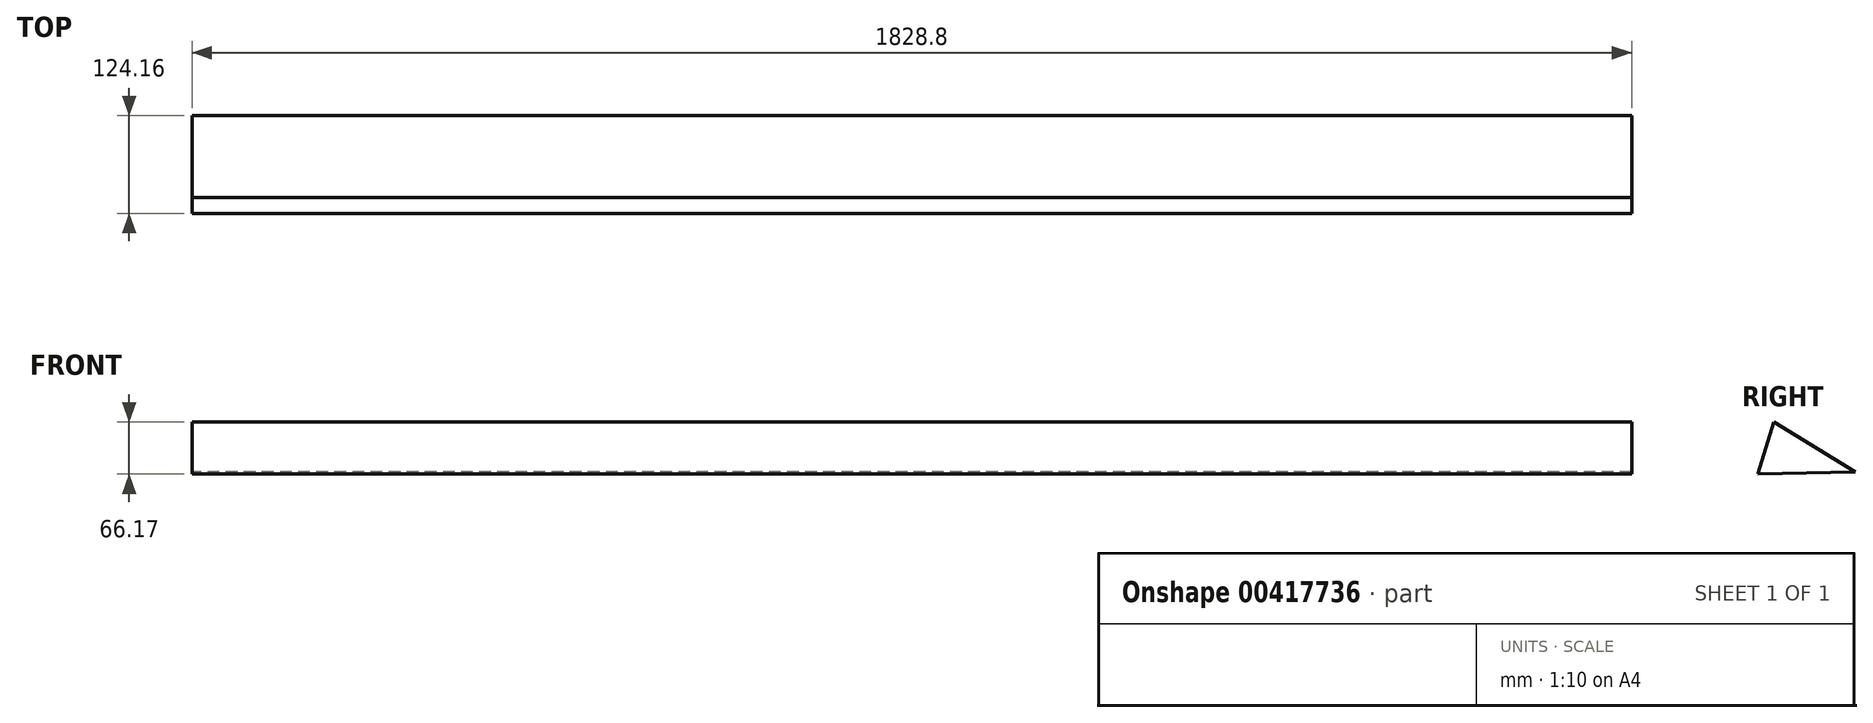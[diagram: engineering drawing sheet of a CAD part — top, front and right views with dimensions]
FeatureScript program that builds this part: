
annotation { "Feature Type Name" : "Feature", "Feature Type Description" : "" }
export const myFeature = defineFeature(function(context is Context, id is Id, definition is map)
    precondition{}
    {
        {
            var Q0;
            Q0=qCreatedBy(makeId("Right.planeOp"),FACE);
            var sketch = newSketch(context, id + "F0", { "sketchPlane" : qUnion([Q0])});
            skLineSegment(sketch, "E0", {"start": v(-31.94, 50.02) * mm, "end": v(-52.36, -16.15) * mm});
            skLineSegment(sketch, "E1", {"start": v(-31.94, 50.02) * mm, "end": v(71.8, -13.35) * mm});
            skLineSegment(sketch, "E2", {"start": v(71.8, -13.35) * mm, "end": v(-52.36, -16.15) * mm});
            skSolve(sketch);
        }
        {
            var Q0;
            Q0=makeQuery(id+"F0.imprint","IMPRINT",FACE,{"disambiguationData":[TD([[makeQuery(id+"F0.imprint","IMPRINT",EDGE,{"derivedFrom":sQuery(id+"F0.wireOp",EDGE,"E0")}),1.0]])]});
            extrude(context, id + "F1", {"entities" : qUnion([Q0]), "depth" : 1828.8 * mm});
        }
    });
